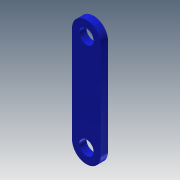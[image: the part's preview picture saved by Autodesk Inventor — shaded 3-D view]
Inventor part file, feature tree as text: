
AUTODESK INVENTOR PART (.ipt)
format: ipt  version: 2013 (Build 170138000, 138)  size: 93,184 bytes
history: native  units: mm
features: sketch x6, extrude x2
ambient origin geometry x8: Origin, YZ Plane, XZ Plane, XY Plane, X Axis, Y Axis, Z Axis, Center Point
bodies: Solid1 (feature_tree)
feature tree (8):
  extrude  "Extrusion1"  Depth=20.0mm
  extrude  "Extrusion2"  Depth=1.5mm TaperAngle=0.0deg
  sketch  "Sketch3"  dims[d5=3.0mm]
  sketch  "Sketch4"  dims[d6=3.0mm]
  sketch  "Sketch5"  dims[d7=2.0mm d8=0.0mm]
  sketch  "Sketch6"
  sketch  "Sketch1"  dims[d0=6.0mm d1=20.0mm]
  sketch  "Sketch2"  dims[d2=6.0mm d3=1.5mm d4=0.0mm]
